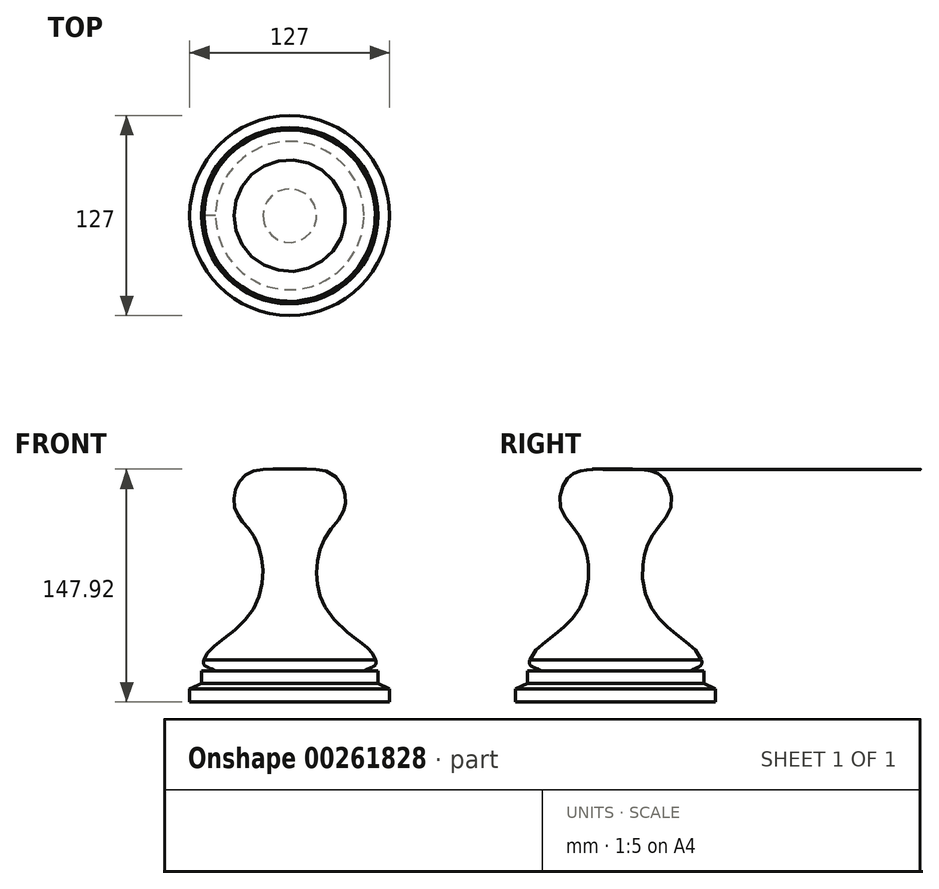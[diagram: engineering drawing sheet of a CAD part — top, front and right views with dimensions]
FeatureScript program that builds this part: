
annotation { "Feature Type Name" : "Feature", "Feature Type Description" : "" }
export const myFeature = defineFeature(function(context is Context, id is Id, definition is map)
    precondition{}
    {
        {
            var Q0;
            Q0=qCreatedBy(makeId("Front.planeOp"),FACE);
            var sketch = newSketch(context, id + "F0", { "sketchPlane" : qUnion([Q0])});
            skLineSegment(sketch, "E0", {"start": v(0, 114.13) * mm, "end": v(0, -114.47) * mm, "construction": true});
            skSolve(sketch);
        }
        {
            var Q0;
            Q0=qCreatedBy(makeId("Front.planeOp"),FACE);
            var sketch = newSketch(context, id + "F1", { "sketchPlane" : qUnion([Q0])});
            skLineSegment(sketch, "E1", {"start": v(0, -73.24) * mm, "end": v(-63.5, -73.24) * mm});
            skLineSegment(sketch, "E2", {"start": v(-63.5, -73.24) * mm, "end": v(-63.5, -64.9) * mm});
            skLineSegment(sketch, "E3", {"start": v(-63.5, -64.9) * mm, "end": v(-56.02, -61.45) * mm});
            skLineSegment(sketch, "E4", {"start": v(-56.02, -61.45) * mm, "end": v(-56.02, -53.66) * mm});
            skLineSegment(sketch, "E5", {"start": v(-56.02, -53.66) * mm, "end": v(-47.1, -53.66) * mm});
            skFitSpline(sketch, "E6", {"points": [v(-47.1, -53.66) * mm, v(-54.45, -46.67) * mm], "startDerivative": vector(-13.37, 8.97) * mm, "endDerivative": vector(4.7, 14) * mm});
            skFitSpline(sketch, "E7", {"points": [v(-54.45, -46.67) * mm, v(-24.45, -16.45) * mm, v(-21.56, 29.56) * mm, v(-34.9, 50) * mm, v(-27.78, 71.12) * mm, v(0, 74.68) * mm], "startDerivative": vector(11.55, 106.86) * mm, "endDerivative": vector(149.07, 9.48) * mm});
            skPoint(sketch, "E8", {"position": v(-51.56, -53.66) * mm});
            skSolve(sketch);
        }
        {
            var Q0;
            Q0 = qSketchRegion(id + "F1", true);
            var Q1;
            Q1=sQuery(id+"F1.wireOp",EDGE,"E7");
            var Q2;
            Q2=sQuery(id+"F1.wireOp",EDGE,"E4");
            var Q3;
            Q3=sQuery(id+"F1.wireOp",EDGE,"E5");
            var Q4;
            Q4=sQuery(id+"F1.wireOp",EDGE,"E6");
            var Q5;
            Q5=sQuery(id+"F1.wireOp",EDGE,"E3");
            var Q6;
            Q6=sQuery(id+"F1.wireOp",EDGE,"E2");
            var Q7;
            Q7=sQuery(id+"F1.wireOp",EDGE,"E1");
            var Q8;
            Q8=sQuery(id+"F0.wireOp",EDGE,"E0");
            revolve(context, id + "F2", {"bodyType" : ToolBodyType.SURFACE, "entities" : qUnion([Q0]), "surfaceEntities" : qUnion([Q1, Q2, Q3, Q4, Q5, Q6, Q7]), "axis" : qUnion([Q8]), "revolveType" : RevolveType.FULL});
        }
    });
